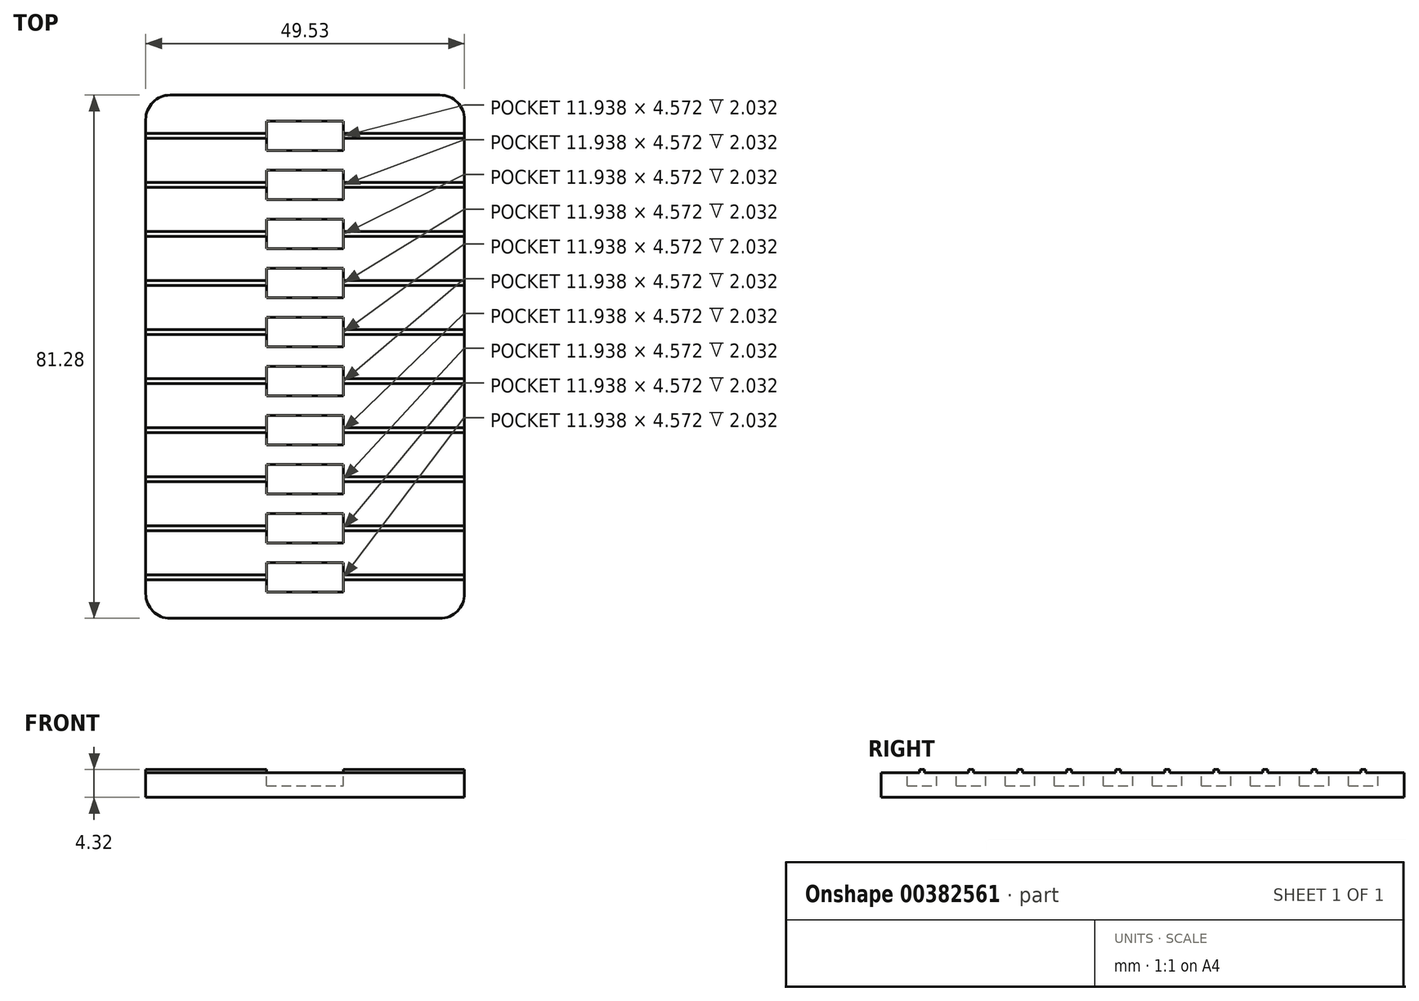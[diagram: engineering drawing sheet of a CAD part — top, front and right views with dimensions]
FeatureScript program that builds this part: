
annotation { "Feature Type Name" : "Feature", "Feature Type Description" : "" }
export const myFeature = defineFeature(function(context is Context, id is Id, definition is map)
    precondition{}
    {
        {
            var Q0;
            Q0=qCreatedBy(makeId("Top.planeOp"),FACE);
            var sketch = newSketch(context, id + "F0", { "sketchPlane" : qUnion([Q0])});
            skLineSegment(sketch, "E0.bottom", {"start": v(0, 0) * mm, "end": v(49.53, 0) * mm});
            skLineSegment(sketch, "E0.top", {"start": v(0, 81.28) * mm, "end": v(49.53, 81.28) * mm});
            skLineSegment(sketch, "E0.left", {"start": v(0, 0) * mm, "end": v(0, 81.28) * mm});
            skLineSegment(sketch, "E0.right", {"start": v(49.53, 0) * mm, "end": v(49.53, 81.28) * mm});
            skSolve(sketch);
        }
        {
            var Q0;
            Q0=qSketchRegion(id+"F0",true);
            extrude(context, id + "F1", {"entities" : qUnion([Q0]), "depth" : 3.8 * mm});
        }
        {
            var Q0;
            Q0=makeQuery(id+"F1.opExtrude","CAP_FACE",FACE,{"disambiguationData":[OSD([sQuery(id+"F0.wireOp",EDGE,"E0.bottom"),sQuery(id+"F0.wireOp",EDGE,"E0.top"),sQuery(id+"F0.wireOp",EDGE,"E0.left"),sQuery(id+"F0.wireOp",EDGE,"E0.right")])],"isStart":false});
            var sketch = newSketch(context, id + "F2", { "sketchPlane" : qUnion([Q0])});
            skLineSegment(sketch, "E1.bottom", {"start": v(18.8, 4.06) * mm, "end": v(30.73, 4.06) * mm});
            skLineSegment(sketch, "E1.top", {"start": v(18.8, 8.64) * mm, "end": v(30.73, 8.64) * mm});
            skLineSegment(sketch, "E1.left", {"start": v(18.8, 4.06) * mm, "end": v(18.8, 8.64) * mm});
            skLineSegment(sketch, "E1.right", {"start": v(30.73, 4.06) * mm, "end": v(30.73, 8.64) * mm});
            skLineSegment(sketch, "E2", {"start": v(30.73, 6.35) * mm, "end": v(49.53, 6.35) * mm, "construction": true});
            skLineSegment(sketch, "E3.0.1.0", {"start": v(18.8, 16.26) * mm, "end": v(30.73, 16.26) * mm});
            skLineSegment(sketch, "E3.0.1.1", {"start": v(18.8, 11.68) * mm, "end": v(30.73, 11.68) * mm});
            skLineSegment(sketch, "E3.0.1.2", {"start": v(30.73, 11.68) * mm, "end": v(30.73, 16.26) * mm});
            skLineSegment(sketch, "E3.0.1.3", {"start": v(18.8, 11.68) * mm, "end": v(18.8, 16.26) * mm});
            skLineSegment(sketch, "E3.0.2.0", {"start": v(18.8, 23.88) * mm, "end": v(30.73, 23.88) * mm});
            skLineSegment(sketch, "E3.0.2.1", {"start": v(18.8, 19.3) * mm, "end": v(30.73, 19.3) * mm});
            skLineSegment(sketch, "E3.0.2.2", {"start": v(30.73, 19.3) * mm, "end": v(30.73, 23.88) * mm});
            skLineSegment(sketch, "E3.0.2.3", {"start": v(18.8, 19.3) * mm, "end": v(18.8, 23.88) * mm});
            skLineSegment(sketch, "E3.0.3.0", {"start": v(18.8, 31.5) * mm, "end": v(30.73, 31.5) * mm});
            skLineSegment(sketch, "E3.0.3.1", {"start": v(18.8, 26.92) * mm, "end": v(30.73, 26.92) * mm});
            skLineSegment(sketch, "E3.0.3.2", {"start": v(30.73, 26.92) * mm, "end": v(30.73, 31.5) * mm});
            skLineSegment(sketch, "E3.0.3.3", {"start": v(18.8, 26.92) * mm, "end": v(18.8, 31.5) * mm});
            skLineSegment(sketch, "E3.0.4.0", {"start": v(18.8, 39.12) * mm, "end": v(30.73, 39.12) * mm});
            skLineSegment(sketch, "E3.0.4.1", {"start": v(18.8, 34.54) * mm, "end": v(30.73, 34.54) * mm});
            skLineSegment(sketch, "E3.0.4.2", {"start": v(30.73, 34.54) * mm, "end": v(30.73, 39.12) * mm});
            skLineSegment(sketch, "E3.0.4.3", {"start": v(18.8, 34.54) * mm, "end": v(18.8, 39.12) * mm});
            skLineSegment(sketch, "E3.0.5.0", {"start": v(18.8, 46.74) * mm, "end": v(30.73, 46.74) * mm});
            skLineSegment(sketch, "E3.0.5.1", {"start": v(18.8, 42.16) * mm, "end": v(30.73, 42.16) * mm});
            skLineSegment(sketch, "E3.0.5.2", {"start": v(30.73, 42.16) * mm, "end": v(30.73, 46.74) * mm});
            skLineSegment(sketch, "E3.0.5.3", {"start": v(18.8, 42.16) * mm, "end": v(18.8, 46.74) * mm});
            skLineSegment(sketch, "E3.0.6.0", {"start": v(18.8, 54.36) * mm, "end": v(30.73, 54.36) * mm});
            skLineSegment(sketch, "E3.0.6.1", {"start": v(18.8, 49.78) * mm, "end": v(30.73, 49.78) * mm});
            skLineSegment(sketch, "E3.0.6.2", {"start": v(30.73, 49.78) * mm, "end": v(30.73, 54.36) * mm});
            skLineSegment(sketch, "E3.0.6.3", {"start": v(18.8, 49.78) * mm, "end": v(18.8, 54.36) * mm});
            skLineSegment(sketch, "E3.0.7.0", {"start": v(18.8, 61.98) * mm, "end": v(30.73, 61.98) * mm});
            skLineSegment(sketch, "E3.0.7.1", {"start": v(18.8, 57.4) * mm, "end": v(30.73, 57.4) * mm});
            skLineSegment(sketch, "E3.0.7.2", {"start": v(30.73, 57.4) * mm, "end": v(30.73, 61.98) * mm});
            skLineSegment(sketch, "E3.0.7.3", {"start": v(18.8, 57.4) * mm, "end": v(18.8, 61.98) * mm});
            skLineSegment(sketch, "E3.0.8.0", {"start": v(18.8, 69.6) * mm, "end": v(30.73, 69.6) * mm});
            skLineSegment(sketch, "E3.0.8.1", {"start": v(18.8, 65.02) * mm, "end": v(30.73, 65.02) * mm});
            skLineSegment(sketch, "E3.0.8.2", {"start": v(30.73, 65.02) * mm, "end": v(30.73, 69.6) * mm});
            skLineSegment(sketch, "E3.0.8.3", {"start": v(18.8, 65.02) * mm, "end": v(18.8, 69.6) * mm});
            skLineSegment(sketch, "E3.0.9.0", {"start": v(18.8, 77.22) * mm, "end": v(30.73, 77.22) * mm});
            skLineSegment(sketch, "E3.0.9.1", {"start": v(18.8, 72.64) * mm, "end": v(30.73, 72.64) * mm});
            skLineSegment(sketch, "E3.0.9.2", {"start": v(30.73, 72.64) * mm, "end": v(30.73, 77.22) * mm});
            skLineSegment(sketch, "E3.0.9.3", {"start": v(18.8, 72.64) * mm, "end": v(18.8, 77.22) * mm});
            skLineSegment(sketch, "E3.direction1", {"start": v(18.8, 4.06) * mm, "end": v(44.2, 4.06) * mm, "construction": true});
            skLineSegment(sketch, "E3.direction2", {"start": v(18.8, 4.06) * mm, "end": v(18.8, 11.68) * mm, "construction": true});
            skSolve(sketch);
        }
        {
            var Q0;
            Q0=qSketchRegion(id+"F2",true);
            extrude(context, id + "F3", {"entities" : qUnion([Q0]), "operationType" : NewBodyOperationType.REMOVE, "oppositeDirection" : true, "depth" : 2.03 * mm});
        }
        {
            var Q0;
            Q0=makeQuery(id+"F1.opExtrude","CAP_FACE",FACE,{"disambiguationData":[OSD([sQuery(id+"F0.wireOp",EDGE,"E0.bottom"),sQuery(id+"F0.wireOp",EDGE,"E0.top"),sQuery(id+"F0.wireOp",EDGE,"E0.left"),sQuery(id+"F0.wireOp",EDGE,"E0.right")])],"isStart":false});
            var sketch = newSketch(context, id + "F4", { "sketchPlane" : qUnion([Q0])});
            skLineSegment(sketch, "E4.bottom", {"start": v(30.73, 5.97) * mm, "end": v(49.53, 5.97) * mm});
            skLineSegment(sketch, "E4.top", {"start": v(30.73, 6.73) * mm, "end": v(49.53, 6.73) * mm});
            skLineSegment(sketch, "E4.left", {"start": v(30.73, 5.97) * mm, "end": v(30.73, 6.73) * mm});
            skLineSegment(sketch, "E4.right", {"start": v(49.53, 5.97) * mm, "end": v(49.53, 6.73) * mm});
            skPoint(sketch, "E5.firstSnap0", {"position": v(40.13, 6.73) * mm});
            skLineSegment(sketch, "E5.bottom", {"start": v(18.8, 6.73) * mm, "end": v(0, 6.73) * mm});
            skLineSegment(sketch, "E5.top", {"start": v(18.8, 5.97) * mm, "end": v(0, 5.97) * mm});
            skLineSegment(sketch, "E5.left", {"start": v(18.8, 6.73) * mm, "end": v(18.8, 5.97) * mm});
            skLineSegment(sketch, "E5.right", {"start": v(0, 6.73) * mm, "end": v(0, 5.97) * mm});
            skLineSegment(sketch, "E6", {"start": v(30.73, 6.35) * mm, "end": v(49.53, 6.35) * mm, "construction": true});
            skLineSegment(sketch, "E7.0.1.0", {"start": v(18.8, 13.59) * mm, "end": v(0, 13.59) * mm});
            skLineSegment(sketch, "E7.0.1.1", {"start": v(30.73, 13.97) * mm, "end": v(49.53, 13.97) * mm, "construction": true});
            skLineSegment(sketch, "E7.0.1.2", {"start": v(18.8, 14.35) * mm, "end": v(0, 14.35) * mm});
            skLineSegment(sketch, "E7.0.1.3", {"start": v(30.73, 14.35) * mm, "end": v(49.53, 14.35) * mm});
            skLineSegment(sketch, "E7.0.1.4", {"start": v(30.73, 13.59) * mm, "end": v(49.53, 13.59) * mm});
            skPoint(sketch, "E7.0.1.5", {"position": v(40.13, 14.35) * mm});
            skLineSegment(sketch, "E7.0.1.6", {"start": v(18.8, 14.35) * mm, "end": v(18.8, 13.59) * mm});
            skLineSegment(sketch, "E7.0.1.7", {"start": v(0, 14.35) * mm, "end": v(0, 13.59) * mm});
            skLineSegment(sketch, "E7.0.1.8", {"start": v(49.53, 13.59) * mm, "end": v(49.53, 14.35) * mm});
            skLineSegment(sketch, "E7.0.1.9", {"start": v(30.73, 13.59) * mm, "end": v(30.73, 14.35) * mm});
            skLineSegment(sketch, "E7.0.2.0", {"start": v(18.8, 21.2) * mm, "end": v(0, 21.2) * mm});
            skLineSegment(sketch, "E7.0.2.1", {"start": v(30.73, 21.6) * mm, "end": v(49.53, 21.6) * mm, "construction": true});
            skLineSegment(sketch, "E7.0.2.2", {"start": v(18.8, 21.97) * mm, "end": v(0, 21.97) * mm});
            skLineSegment(sketch, "E7.0.2.3", {"start": v(30.73, 21.97) * mm, "end": v(49.53, 21.97) * mm});
            skLineSegment(sketch, "E7.0.2.4", {"start": v(30.73, 21.2) * mm, "end": v(49.53, 21.2) * mm});
            skPoint(sketch, "E7.0.2.5", {"position": v(40.13, 21.97) * mm});
            skLineSegment(sketch, "E7.0.2.6", {"start": v(18.8, 21.97) * mm, "end": v(18.8, 21.2) * mm});
            skLineSegment(sketch, "E7.0.2.7", {"start": v(0, 21.97) * mm, "end": v(0, 21.2) * mm});
            skLineSegment(sketch, "E7.0.2.8", {"start": v(49.53, 21.2) * mm, "end": v(49.53, 21.97) * mm});
            skLineSegment(sketch, "E7.0.2.9", {"start": v(30.73, 21.2) * mm, "end": v(30.73, 21.97) * mm});
            skLineSegment(sketch, "E7.0.3.0", {"start": v(18.8, 28.83) * mm, "end": v(0, 28.83) * mm});
            skLineSegment(sketch, "E7.0.3.1", {"start": v(30.73, 29.21) * mm, "end": v(49.53, 29.21) * mm, "construction": true});
            skLineSegment(sketch, "E7.0.3.2", {"start": v(18.8, 29.6) * mm, "end": v(0, 29.6) * mm});
            skLineSegment(sketch, "E7.0.3.3", {"start": v(30.73, 29.6) * mm, "end": v(49.53, 29.6) * mm});
            skLineSegment(sketch, "E7.0.3.4", {"start": v(30.73, 28.83) * mm, "end": v(49.53, 28.83) * mm});
            skPoint(sketch, "E7.0.3.5", {"position": v(40.13, 29.6) * mm});
            skLineSegment(sketch, "E7.0.3.6", {"start": v(18.8, 29.6) * mm, "end": v(18.8, 28.83) * mm});
            skLineSegment(sketch, "E7.0.3.7", {"start": v(0, 29.6) * mm, "end": v(0, 28.83) * mm});
            skLineSegment(sketch, "E7.0.3.8", {"start": v(49.53, 28.83) * mm, "end": v(49.53, 29.6) * mm});
            skLineSegment(sketch, "E7.0.3.9", {"start": v(30.73, 28.83) * mm, "end": v(30.73, 29.6) * mm});
            skLineSegment(sketch, "E7.0.4.0", {"start": v(18.8, 36.45) * mm, "end": v(0, 36.45) * mm});
            skLineSegment(sketch, "E7.0.4.1", {"start": v(30.73, 36.83) * mm, "end": v(49.53, 36.83) * mm, "construction": true});
            skLineSegment(sketch, "E7.0.4.2", {"start": v(18.8, 37.21) * mm, "end": v(0, 37.21) * mm});
            skLineSegment(sketch, "E7.0.4.3", {"start": v(30.73, 37.21) * mm, "end": v(49.53, 37.21) * mm});
            skLineSegment(sketch, "E7.0.4.4", {"start": v(30.73, 36.45) * mm, "end": v(49.53, 36.45) * mm});
            skPoint(sketch, "E7.0.4.5", {"position": v(40.13, 37.21) * mm});
            skLineSegment(sketch, "E7.0.4.6", {"start": v(18.8, 37.21) * mm, "end": v(18.8, 36.45) * mm});
            skLineSegment(sketch, "E7.0.4.7", {"start": v(0, 37.21) * mm, "end": v(0, 36.45) * mm});
            skLineSegment(sketch, "E7.0.4.8", {"start": v(49.53, 36.45) * mm, "end": v(49.53, 37.21) * mm});
            skLineSegment(sketch, "E7.0.4.9", {"start": v(30.73, 36.45) * mm, "end": v(30.73, 37.21) * mm});
            skLineSegment(sketch, "E7.0.5.0", {"start": v(18.8, 44.07) * mm, "end": v(0, 44.07) * mm});
            skLineSegment(sketch, "E7.0.5.1", {"start": v(30.73, 44.45) * mm, "end": v(49.53, 44.45) * mm, "construction": true});
            skLineSegment(sketch, "E7.0.5.2", {"start": v(18.8, 44.83) * mm, "end": v(0, 44.83) * mm});
            skLineSegment(sketch, "E7.0.5.3", {"start": v(30.73, 44.83) * mm, "end": v(49.53, 44.83) * mm});
            skLineSegment(sketch, "E7.0.5.4", {"start": v(30.73, 44.07) * mm, "end": v(49.53, 44.07) * mm});
            skPoint(sketch, "E7.0.5.5", {"position": v(40.13, 44.83) * mm});
            skLineSegment(sketch, "E7.0.5.6", {"start": v(18.8, 44.83) * mm, "end": v(18.8, 44.07) * mm});
            skLineSegment(sketch, "E7.0.5.7", {"start": v(0, 44.83) * mm, "end": v(0, 44.07) * mm});
            skLineSegment(sketch, "E7.0.5.8", {"start": v(49.53, 44.07) * mm, "end": v(49.53, 44.83) * mm});
            skLineSegment(sketch, "E7.0.5.9", {"start": v(30.73, 44.07) * mm, "end": v(30.73, 44.83) * mm});
            skLineSegment(sketch, "E7.0.6.0", {"start": v(18.8, 51.69) * mm, "end": v(0, 51.69) * mm});
            skLineSegment(sketch, "E7.0.6.1", {"start": v(30.73, 52.07) * mm, "end": v(49.53, 52.07) * mm, "construction": true});
            skLineSegment(sketch, "E7.0.6.2", {"start": v(18.8, 52.45) * mm, "end": v(0, 52.45) * mm});
            skLineSegment(sketch, "E7.0.6.3", {"start": v(30.73, 52.45) * mm, "end": v(49.53, 52.45) * mm});
            skLineSegment(sketch, "E7.0.6.4", {"start": v(30.73, 51.69) * mm, "end": v(49.53, 51.69) * mm});
            skPoint(sketch, "E7.0.6.5", {"position": v(40.13, 52.45) * mm});
            skLineSegment(sketch, "E7.0.6.6", {"start": v(18.8, 52.45) * mm, "end": v(18.8, 51.69) * mm});
            skLineSegment(sketch, "E7.0.6.7", {"start": v(0, 52.45) * mm, "end": v(0, 51.69) * mm});
            skLineSegment(sketch, "E7.0.6.8", {"start": v(49.53, 51.69) * mm, "end": v(49.53, 52.45) * mm});
            skLineSegment(sketch, "E7.0.6.9", {"start": v(30.73, 51.69) * mm, "end": v(30.73, 52.45) * mm});
            skLineSegment(sketch, "E7.0.7.0", {"start": v(18.8, 59.3) * mm, "end": v(0, 59.3) * mm});
            skLineSegment(sketch, "E7.0.7.1", {"start": v(30.73, 59.69) * mm, "end": v(49.53, 59.69) * mm, "construction": true});
            skLineSegment(sketch, "E7.0.7.2", {"start": v(18.8, 60.07) * mm, "end": v(0, 60.07) * mm});
            skLineSegment(sketch, "E7.0.7.3", {"start": v(30.73, 60.07) * mm, "end": v(49.53, 60.07) * mm});
            skLineSegment(sketch, "E7.0.7.4", {"start": v(30.73, 59.3) * mm, "end": v(49.53, 59.3) * mm});
            skPoint(sketch, "E7.0.7.5", {"position": v(40.13, 60.07) * mm});
            skLineSegment(sketch, "E7.0.7.6", {"start": v(18.8, 60.07) * mm, "end": v(18.8, 59.3) * mm});
            skLineSegment(sketch, "E7.0.7.7", {"start": v(0, 60.07) * mm, "end": v(0, 59.3) * mm});
            skLineSegment(sketch, "E7.0.7.8", {"start": v(49.53, 59.3) * mm, "end": v(49.53, 60.07) * mm});
            skLineSegment(sketch, "E7.0.7.9", {"start": v(30.73, 59.3) * mm, "end": v(30.73, 60.07) * mm});
            skLineSegment(sketch, "E7.0.8.0", {"start": v(18.8, 66.93) * mm, "end": v(0, 66.93) * mm});
            skLineSegment(sketch, "E7.0.8.1", {"start": v(30.73, 67.3) * mm, "end": v(49.53, 67.3) * mm, "construction": true});
            skLineSegment(sketch, "E7.0.8.2", {"start": v(18.8, 67.7) * mm, "end": v(0, 67.7) * mm});
            skLineSegment(sketch, "E7.0.8.3", {"start": v(30.73, 67.7) * mm, "end": v(49.53, 67.7) * mm});
            skLineSegment(sketch, "E7.0.8.4", {"start": v(30.73, 66.93) * mm, "end": v(49.53, 66.93) * mm});
            skPoint(sketch, "E7.0.8.5", {"position": v(40.13, 67.7) * mm});
            skLineSegment(sketch, "E7.0.8.6", {"start": v(18.8, 67.7) * mm, "end": v(18.8, 66.93) * mm});
            skLineSegment(sketch, "E7.0.8.7", {"start": v(0, 67.7) * mm, "end": v(0, 66.93) * mm});
            skLineSegment(sketch, "E7.0.8.8", {"start": v(49.53, 66.93) * mm, "end": v(49.53, 67.7) * mm});
            skLineSegment(sketch, "E7.0.8.9", {"start": v(30.73, 66.93) * mm, "end": v(30.73, 67.7) * mm});
            skLineSegment(sketch, "E7.0.9.0", {"start": v(18.8, 74.55) * mm, "end": v(0, 74.55) * mm});
            skLineSegment(sketch, "E7.0.9.1", {"start": v(30.73, 74.93) * mm, "end": v(49.53, 74.93) * mm, "construction": true});
            skLineSegment(sketch, "E7.0.9.2", {"start": v(18.8, 75.31) * mm, "end": v(0, 75.31) * mm});
            skLineSegment(sketch, "E7.0.9.3", {"start": v(30.73, 75.31) * mm, "end": v(49.53, 75.31) * mm});
            skLineSegment(sketch, "E7.0.9.4", {"start": v(30.73, 74.55) * mm, "end": v(49.53, 74.55) * mm});
            skPoint(sketch, "E7.0.9.5", {"position": v(40.13, 75.31) * mm});
            skLineSegment(sketch, "E7.0.9.6", {"start": v(18.8, 75.31) * mm, "end": v(18.8, 74.55) * mm});
            skLineSegment(sketch, "E7.0.9.7", {"start": v(0, 75.31) * mm, "end": v(0, 74.55) * mm});
            skLineSegment(sketch, "E7.0.9.8", {"start": v(49.53, 74.55) * mm, "end": v(49.53, 75.31) * mm});
            skLineSegment(sketch, "E7.0.9.9", {"start": v(30.73, 74.55) * mm, "end": v(30.73, 75.31) * mm});
            skLineSegment(sketch, "E7.direction1", {"start": v(0, 5.97) * mm, "end": v(25.4, 5.97) * mm, "construction": true});
            skLineSegment(sketch, "E7.direction2", {"start": v(0, 5.97) * mm, "end": v(0, 13.59) * mm, "construction": true});
            skSolve(sketch);
        }
        {
            var Q0;
            Q0=qSketchRegion(id+"F4",true);
            extrude(context, id + "F5", {"entities" : qUnion([Q0]), "operationType" : NewBodyOperationType.ADD, "depth" : 0.5 * mm});
        }
        {
            var Q0;
            Q0=makeQuery(id+"F1.opExtrude","SWEPT_EDGE",EDGE,{"disambiguationData":[OSD([sQuery(id+"F0.wireOp",EDGE,"E0.bottom"),sQuery(id+"F0.wireOp",EDGE,"E0.right")])]});
            var Q1;
            Q1=makeQuery(id+"F1.opExtrude","SWEPT_EDGE",EDGE,{"disambiguationData":[OSD([sQuery(id+"F0.wireOp",EDGE,"E0.bottom"),sQuery(id+"F0.wireOp",EDGE,"E0.left")])]});
            var Q2;
            Q2=makeQuery(id+"F1.opExtrude","SWEPT_EDGE",EDGE,{"disambiguationData":[OSD([sQuery(id+"F0.wireOp",EDGE,"E0.top"),sQuery(id+"F0.wireOp",EDGE,"E0.left")])]});
            var Q3;
            Q3=makeQuery(id+"F1.opExtrude","SWEPT_EDGE",EDGE,{"disambiguationData":[OSD([sQuery(id+"F0.wireOp",EDGE,"E0.top"),sQuery(id+"F0.wireOp",EDGE,"E0.right")])]});
            fillet(context, id + "F6", {"entities" : qUnion([Q0, Q1, Q2, Q3]), "radius" : 3.8 * mm, "tangentPropagation" : true, "allowEdgeOverflow" : false});
        }
    });
